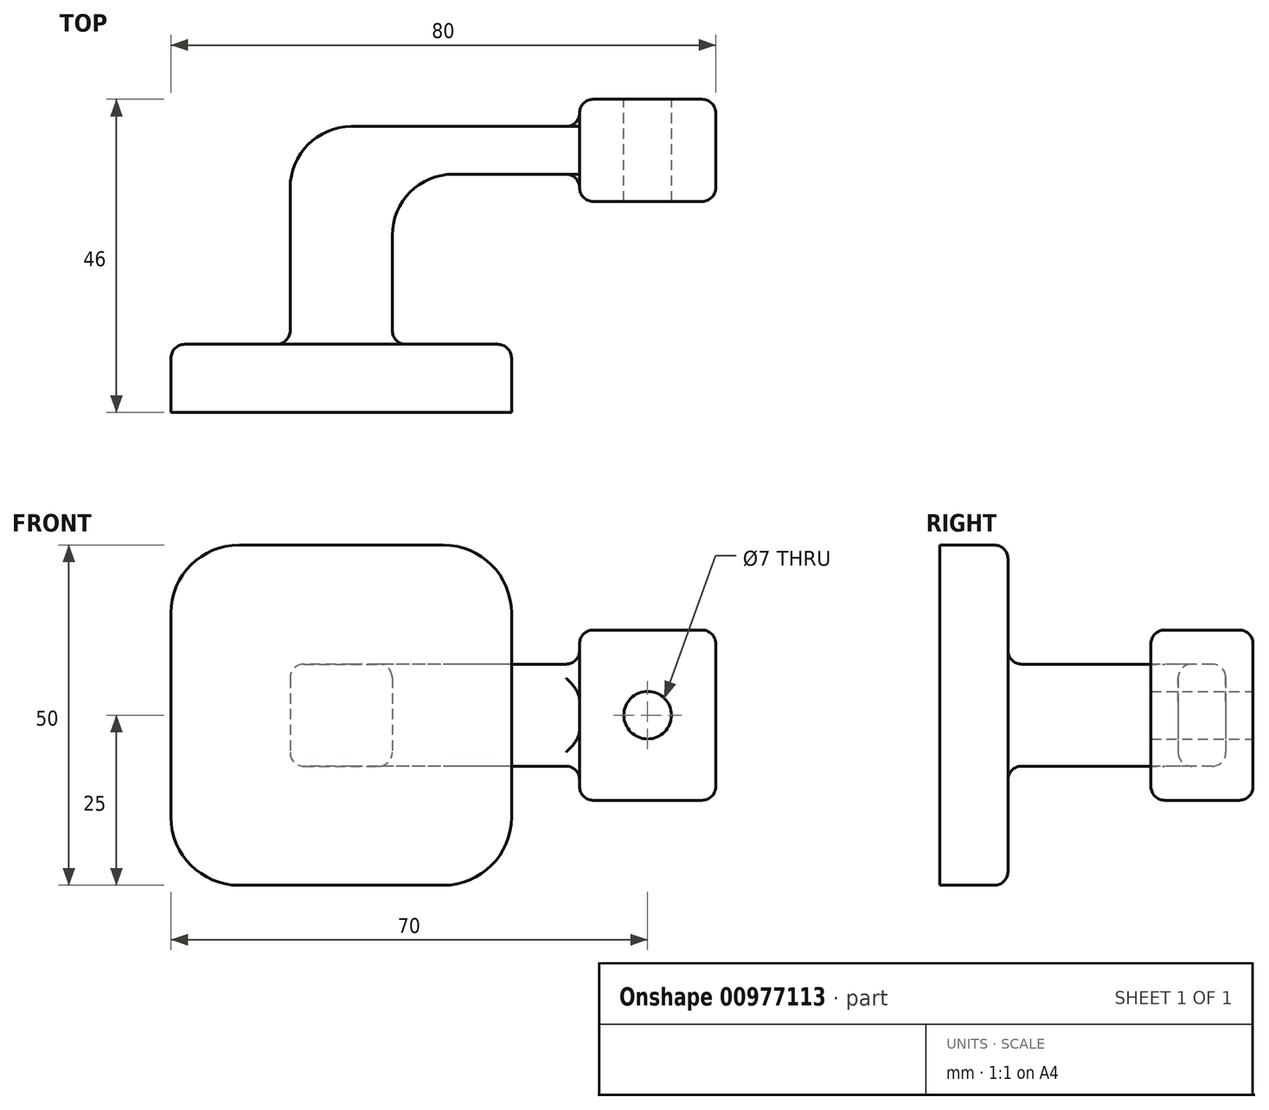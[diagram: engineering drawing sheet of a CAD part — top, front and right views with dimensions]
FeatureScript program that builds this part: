
annotation { "Feature Type Name" : "Feature", "Feature Type Description" : "" }
export const myFeature = defineFeature(function(context is Context, id is Id, definition is map)
    precondition{}
    {
        {
            var Q0;
            Q0=qCreatedBy(makeId("Top.planeOp"),FACE);
            var sketch = newSketch(context, id + "F0", { "sketchPlane" : qUnion([Q0])});
            skLineSegment(sketch, "E0.bottom", {"start": v(-50, 5) * mm, "end": v(0, 5) * mm});
            skLineSegment(sketch, "E0.top", {"start": v(-50, -5) * mm, "end": v(0, -5) * mm});
            skLineSegment(sketch, "E0.left", {"start": v(-50, 5) * mm, "end": v(-50, -5) * mm});
            skLineSegment(sketch, "E0.right", {"start": v(0, 5) * mm, "end": v(0, -5) * mm});
            skLineSegment(sketch, "E1.bottom", {"start": v(10, 41) * mm, "end": v(30, 41) * mm});
            skLineSegment(sketch, "E1.top", {"start": v(10, 26) * mm, "end": v(30, 26) * mm});
            skLineSegment(sketch, "E1.left", {"start": v(10, 41) * mm, "end": v(10, 26) * mm});
            skLineSegment(sketch, "E1.right", {"start": v(30, 41) * mm, "end": v(30, 26) * mm});
            skLineSegment(sketch, "E2", {"start": v(-32.5, 5) * mm, "end": v(-32.5, 28) * mm});
            skLineSegment(sketch, "E3", {"start": v(10, 37) * mm, "end": v(-23.5, 37) * mm});
            skLineSegment(sketch, "E4", {"start": v(10, 30) * mm, "end": v(-8.5, 30) * mm});
            skLineSegment(sketch, "E5", {"start": v(-17.5, 5) * mm, "end": v(-17.5, 21) * mm});
            skArc(sketch, "E6", {"start": v(-23.5, 37) * mm, "mid": v(-29.86, 34.36) * mm, "end": v(-32.5, 28) * mm});
            skArc(sketch, "E7", {"start": v(-8.5, 30) * mm, "mid": v(-14.86, 27.36) * mm, "end": v(-17.5, 21) * mm});
            skLineSegment(sketch, "E8", {"start": v(-25, 5) * mm, "end": v(-25, -5) * mm, "construction": true});
            skLineSegment(sketch, "E9", {"start": v(10, 33.5) * mm, "end": v(30, 33.5) * mm, "construction": true});
            skSolve(sketch);
        }
        {
            var Q0;
            Q0=makeQuery(id+"F0.imprint","IMPRINT",FACE,{"disambiguationData":[TD([[makeQuery(id+"F0.imprint","IMPRINT",EDGE,{"derivedFrom":sQuery(id+"F0.wireOp",EDGE,"E0.top")}),1.0]])]});
            extrude(context, id + "F1", {"entities" : qUnion([Q0]), "endBound" : BoundingType.SYMMETRIC, "oppositeDirection" : true, "depth" : 50 * mm, "offsetDistance" : 25 * mm});
        }
        {
            var Q0;
            {var subQ1=sQuery(id+"F0.wireOp",EDGE,"E2");Q0=makeQuery(id+"F0.imprint","IMPRINT",FACE,{"disambiguationData":[TD([[makeQuery(id+"F0.imprint","IMPRINT",EDGE,{"derivedFrom":subQ1}),-1.0]])]});}
            extrude(context, id + "F2", {"entities" : qUnion([Q0]), "operationType" : NewBodyOperationType.ADD, "endBound" : BoundingType.SYMMETRIC, "depth" : 15 * mm, "offsetDistance" : 25 * mm});
        }
        {
            var Q0;
            {var subQ3=sQuery(id+"F0.wireOp",EDGE,"E1.bottom");Q0=makeQuery(id+"F0.imprint","IMPRINT",FACE,{"disambiguationData":[TD([[makeQuery(id+"F0.imprint","IMPRINT",EDGE,{"derivedFrom":subQ3}),-1.0]])]});}
            extrude(context, id + "F3", {"entities" : qUnion([Q0]), "operationType" : NewBodyOperationType.ADD, "endBound" : BoundingType.SYMMETRIC, "depth" : 25 * mm, "offsetDistance" : 25 * mm});
        }
        {
            var Q0;
            Q0=makeQuery(id+"F1.opExtrude","CAP_EDGE",EDGE,{"disambiguationData":[OSD([sQuery(id+"F0.wireOp",EDGE,"E0.left")])],"isStart":true});
            var Q1;
            Q1=makeQuery(id+"F1.opExtrude","CAP_EDGE",EDGE,{"disambiguationData":[OSD([sQuery(id+"F0.wireOp",EDGE,"E0.right")])],"isStart":true});
            var Q2;
            Q2=makeQuery(id+"F1.opExtrude","CAP_EDGE",EDGE,{"disambiguationData":[OSD([sQuery(id+"F0.wireOp",EDGE,"E0.right")])],"isStart":false});
            var Q3;
            Q3=makeQuery(id+"F1.opExtrude","CAP_EDGE",EDGE,{"disambiguationData":[OSD([sQuery(id+"F0.wireOp",EDGE,"E0.left")])],"isStart":false});
            fillet(context, id + "F4", {"entities" : qUnion([Q0, Q1, Q2, Q3]), "radius" : 10 * mm, "tangentPropagation" : true, "allowEdgeOverflow" : false});
        }
        {
            var Q0;
            Q0=makeQuery(id+"F2.opExtrude","CAP_FACE",FACE,{"disambiguationData":[OSD([sQuery(id+"F0.wireOp",EDGE,"E0.bottom"),sQuery(id+"F0.wireOp",EDGE,"E1.left"),sQuery(id+"F0.wireOp",EDGE,"E2"),sQuery(id+"F0.wireOp",EDGE,"E3"),sQuery(id+"F0.wireOp",EDGE,"E4"),sQuery(id+"F0.wireOp",EDGE,"E5"),sQuery(id+"F0.wireOp",EDGE,"E6"),sQuery(id+"F0.wireOp",EDGE,"E7")])],"isStart":false});
            var Q1;
            Q1=makeQuery(id+"F2.opExtrude","CAP_FACE",FACE,{"disambiguationData":[OSD([sQuery(id+"F0.wireOp",EDGE,"E0.bottom"),sQuery(id+"F0.wireOp",EDGE,"E1.left"),sQuery(id+"F0.wireOp",EDGE,"E2"),sQuery(id+"F0.wireOp",EDGE,"E3"),sQuery(id+"F0.wireOp",EDGE,"E4"),sQuery(id+"F0.wireOp",EDGE,"E5"),sQuery(id+"F0.wireOp",EDGE,"E6"),sQuery(id+"F0.wireOp",EDGE,"E7")])],"isStart":true});
            var Q2;
            Q2=makeQuery(id+"F1.opExtrude","SWEPT_FACE",FACE,{"disambiguationData":[OSD([sQuery(id+"F0.wireOp",EDGE,"E0.bottom")])]});
            fillet(context, id + "F5", {"entities" : qUnion([Q0, Q1, Q2]), "radius" : 2 * mm, "tangentPropagation" : true, "allowEdgeOverflow" : false});
        }
        {
            var Q0;
            Q0=makeQuery(id+"F3.opExtrude","SWEPT_FACE",FACE,{"disambiguationData":[OSD([sQuery(id+"F0.wireOp",EDGE,"E1.bottom")])]});
            var sketch = newSketch(context, id + "F6", { "sketchPlane" : qUnion([Q0])});
            skCircle(sketch, "E10", {"center": v(-20, 0) * mm, "radius": 3.5 * mm});
            skPoint(sketch, "E10.centerSnap0", {"position": v(-20, 12.5) * mm});
            skSolve(sketch);
        }
        {
            var Q0;
            Q0 = qSketchRegion(id + "F6", true);
            var Q1;
            Q1=makeQuery(id+"F3.opExtrude","SWEPT_FACE",FACE,{"disambiguationData":[OSD([sQuery(id+"F0.wireOp",EDGE,"E1.top")])]});
            extrude(context, id + "F7", {"entities" : qUnion([Q0]), "operationType" : NewBodyOperationType.REMOVE, "endBound" : BoundingType.UP_TO_SURFACE, "oppositeDirection" : true, "depth" : 25 * mm, "endBoundEntityFace" : qUnion([Q1]), "offsetDistance" : 25 * mm});
        }
        {
            var Q0;
            Q0=makeQuery(id+"F3.opExtrude","CAP_FACE",FACE,{"disambiguationData":[OSD([sQuery(id+"F0.wireOp",EDGE,"E1.bottom"),sQuery(id+"F0.wireOp",EDGE,"E1.top"),sQuery(id+"F0.wireOp",EDGE,"E1.left"),sQuery(id+"F0.wireOp",EDGE,"E1.right")])],"isStart":true});
            var Q1;
            Q1=makeQuery(id+"F3.opExtrude","CAP_FACE",FACE,{"disambiguationData":[OSD([sQuery(id+"F0.wireOp",EDGE,"E1.bottom"),sQuery(id+"F0.wireOp",EDGE,"E1.top"),sQuery(id+"F0.wireOp",EDGE,"E1.left"),sQuery(id+"F0.wireOp",EDGE,"E1.right")])],"isStart":false});
            var Q2;
            Q2=makeQuery(id+"F3.opExtrude","SWEPT_FACE",FACE,{"disambiguationData":[OSD([sQuery(id+"F0.wireOp",EDGE,"E1.right")])]});
            var Q3;
            Q3=makeQuery(id+"F3.opExtrude","SWEPT_EDGE",EDGE,{"disambiguationData":[OSD([sQuery(id+"F0.wireOp",EDGE,"E1.bottom"),sQuery(id+"F0.wireOp",EDGE,"E1.left")])]});
            var Q4;
            Q4=makeQuery(id+"F3.opExtrude","SWEPT_EDGE",EDGE,{"disambiguationData":[OSD([sQuery(id+"F0.wireOp",EDGE,"E1.top"),sQuery(id+"F0.wireOp",EDGE,"E1.left")])]});
            fillet(context, id + "F8", {"entities" : qUnion([Q0, Q1, Q2, Q3, Q4]), "radius" : 2 * mm, "tangentPropagation" : true, "allowEdgeOverflow" : false});
        }
    });
